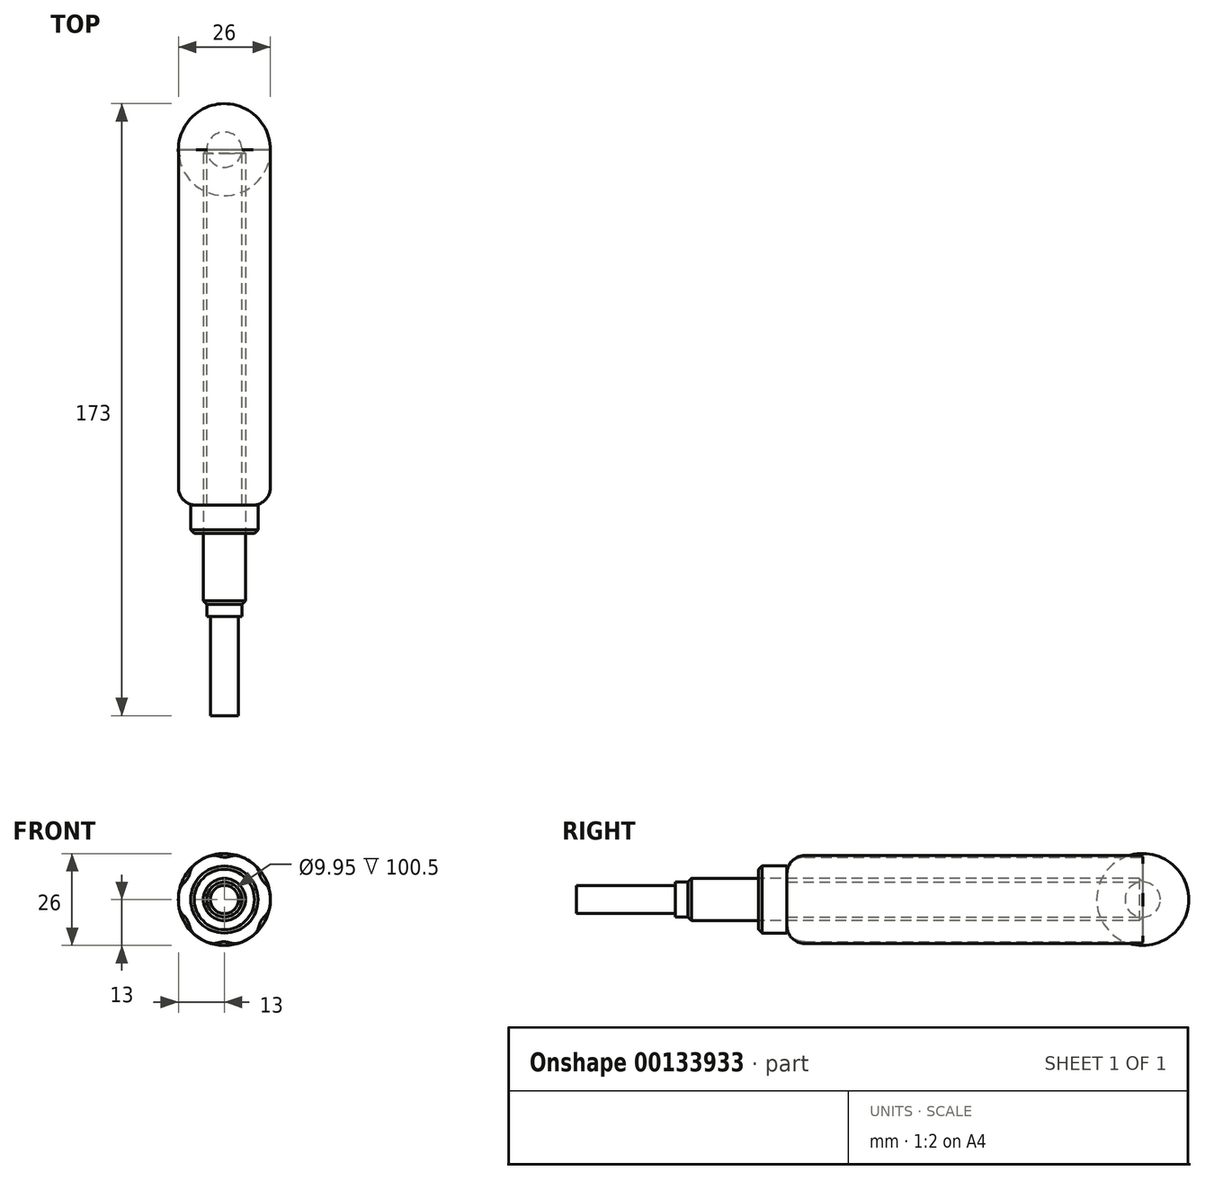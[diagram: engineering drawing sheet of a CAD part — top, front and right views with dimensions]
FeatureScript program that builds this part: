
annotation { "Feature Type Name" : "Feature", "Feature Type Description" : "" }
export const myFeature = defineFeature(function(context is Context, id is Id, definition is map)
    precondition{}
    {
        {
            var Q0;
            Q0=qCreatedBy(makeId("Front.planeOp"),FACE);
            var sketch = newSketch(context, id + "F0", { "sketchPlane" : qUnion([Q0])});
            skCircle(sketch, "E0", {"center": v(0, 0) * mm, "radius": 3.98 * mm});
            skSolve(sketch);
        }
        {
            var Q0;
            Q0 = qSketchRegion(id + "F0", true);
            extrude(context, id + "F1", {"entities" : qUnion([Q0]), "oppositeDirection" : true, "depth" : 28 * mm});
        }
        {
            var Q0;
            Q0=makeQuery(id+"F1.opExtrude","CAP_FACE",FACE,{"disambiguationData":[OSD([sQuery(id+"F0.wireOp",EDGE,"E0")])],"isStart":false});
            var sketch = newSketch(context, id + "F2", { "sketchPlane" : qUnion([Q0])});
            skCircle(sketch, "E1", {"center": v(0, 0) * mm, "radius": 4.92 * mm});
            skSolve(sketch);
        }
        {
            var Q0;
            Q0 = qSketchRegion(id + "F2", true);
            extrude(context, id + "F3", {"entities" : qUnion([Q0]), "operationType" : NewBodyOperationType.ADD, "depth" : 3.5 * mm});
        }
        {
            var Q0;
            Q0=makeQuery(id+"F3.opExtrude","CAP_FACE",FACE,{"disambiguationData":[OSD([sQuery(id+"F2.wireOp",EDGE,"E1")])],"isStart":false});
            var sketch = newSketch(context, id + "F4", { "sketchPlane" : qUnion([Q0])});
            skCircle(sketch, "E2", {"center": v(0, 0) * mm, "radius": 5.97 * mm});
            skSolve(sketch);
        }
        {
            var Q0;
            Q0 = qSketchRegion(id + "F4", true);
            extrude(context, id + "F5", {"entities" : qUnion([Q0]), "operationType" : NewBodyOperationType.ADD, "depth" : 128.5 * mm});
        }
        {
            var Q0;
            Q0=makeQuery(id+"F5.opExtrude","SWEPT_FACE",FACE,{"disambiguationData":[OSD([sQuery(id+"F4.wireOp",EDGE,"E2")])]});
            chamfer(context, id + "F6", {"entities" : qUnion([Q0]), "chamferType" : ChamferType.OFFSET_ANGLE, "width" : 1 * mm, "oppositeDirection" : false, "angle" : 45 * degree, "tangentPropagation" : true});
        }
        {
            var Q0;
            Q0=makeQuery(id+"F5.opExtrude","CAP_FACE",FACE,{"disambiguationData":[OSD([sQuery(id+"F4.wireOp",EDGE,"E2")])],"isStart":false});
            var sketch = newSketch(context, id + "F7", { "sketchPlane" : qUnion([Q0])});
            skCircle(sketch, "E3", {"center": v(0, 0) * mm, "radius": 13 * mm});
            skArc(sketch, "E4", {"start": v(-2.72, 12.71) * mm, "mid": v(-0.07, 11.97) * mm, "end": v(2.57, 12.74) * mm});
            skArc(sketch, "E5.1.0", {"start": v(-12.37, 4) * mm, "mid": v(-10.4, 5.93) * mm, "end": v(-9.75, 8.6) * mm});
            skArc(sketch, "E5.2.0", {"start": v(-9.65, -8.71) * mm, "mid": v(-10.33, -6.04) * mm, "end": v(-12.32, -4.14) * mm});
            skArc(sketch, "E5.3.0", {"start": v(2.72, -12.71) * mm, "mid": v(0.07, -11.97) * mm, "end": v(-2.57, -12.74) * mm});
            skArc(sketch, "E5.4.0", {"start": v(12.37, -4) * mm, "mid": v(10.4, -5.93) * mm, "end": v(9.75, -8.6) * mm});
            skArc(sketch, "E5.5.0", {"start": v(9.65, 8.71) * mm, "mid": v(10.33, 6.04) * mm, "end": v(12.32, 4.14) * mm});
            skSolve(sketch);
        }
        {
            var Q0;
            {var subQ5=sQuery(id+"F7.wireOp",EDGE,"E4");Q0=makeQuery(id+"F7.imprint","IMPRINT",FACE,{"disambiguationData":[TD([[makeQuery(id+"F7.imprint","IMPRINT",EDGE,{"derivedFrom":subQ5}),-1.0]])]});}
            extrude(context, id + "F8", {"entities" : qUnion([Q0]), "oppositeDirection" : true, "depth" : 100.5 * mm});
        }
        {
            var Q0;
            Q0=makeQuery(id+"F8.opExtrude","CAP_FACE",FACE,{"disambiguationData":[OSD([sQuery(id+"F4.wireOp",EDGE,"E2"),sQuery(id+"F7.wireOp",EDGE,"E3"),sQuery(id+"F7.wireOp",EDGE,"E4"),sQuery(id+"F7.wireOp",EDGE,"E5.1.0"),sQuery(id+"F7.wireOp",EDGE,"E5.2.0"),sQuery(id+"F7.wireOp",EDGE,"E5.3.0"),sQuery(id+"F7.wireOp",EDGE,"E5.4.0"),sQuery(id+"F7.wireOp",EDGE,"E5.5.0")])],"isStart":false});
            var sketch = newSketch(context, id + "F9", { "sketchPlane" : qUnion([Q0])});
            skCircle(sketch, "E6", {"center": v(0, 0) * mm, "radius": 9.5 * mm});
            skSolve(sketch);
        }
        {
            var Q0;
            Q0 = qSketchRegion(id + "F9", true);
            extrude(context, id + "F10", {"entities" : qUnion([Q0]), "depth" : 8 * mm});
        }
        {
            var Q0;
            Q0=makeQuery(id+"F10.opExtrude","CAP_EDGE",EDGE,{"disambiguationData":[OSD([sQuery(id+"F9.wireOp",EDGE,"E6")])],"isStart":false});
            chamfer(context, id + "F11", {"entities" : qUnion([Q0]), "width" : 1 * mm, "tangentPropagation" : true});
        }
        {
            var Q0;
            {var subQ0=sQuery(id+"F4.wireOp",EDGE,"E2");Q0=makeQuery(id+"F8.boolean.opBoolean","MERGE",FACE,{"derivedFrom":[makeQuery(id+"F5.opExtrude","CAP_FACE",FACE,{"disambiguationData":[OSD([subQ0])],"isStart":false}),makeQuery(id+"F8.opExtrude","CAP_FACE",FACE,{"disambiguationData":[OSD([subQ0,sQuery(id+"F7.wireOp",EDGE,"E3"),sQuery(id+"F7.wireOp",EDGE,"E4"),sQuery(id+"F7.wireOp",EDGE,"E5.1.0"),sQuery(id+"F7.wireOp",EDGE,"E5.2.0"),sQuery(id+"F7.wireOp",EDGE,"E5.3.0"),sQuery(id+"F7.wireOp",EDGE,"E5.4.0"),sQuery(id+"F7.wireOp",EDGE,"E5.5.0")])],"isStart":true})]});}
            var sketch = newSketch(context, id + "F12", { "sketchPlane" : qUnion([Q0])});
            skCircle(sketch, "E7", {"center": v(0, 0) * mm, "radius": 13 * mm});
            skLineSegment(sketch, "E8", {"start": v(-13, -0.07) * mm, "end": v(13, 0.07) * mm, "construction": true});
            skLineSegment(sketch, "E9", {"start": v(-13, -0.07) * mm, "end": v(13, 0.07) * mm});
            skSolve(sketch);
        }
        {
            var Q0;
            {var subQ2=sQuery(id+"F12.wireOp",EDGE,"E9");Q0=makeQuery(id+"F12.imprint","IMPRINT",FACE,{"disambiguationData":[TD([[makeQuery(id+"F12.imprint","IMPRINT",EDGE,{"derivedFrom":subQ2}),-1.0]])]});}
            var Q1;
            {var subQ1=makeQuery(id+"F8.opExtrude","CAP_EDGE",EDGE,{"disambiguationData":[OSD([sQuery(id+"F7.wireOp",EDGE,"E5.4.0")])],"isStart":true});Q1=makeQuery(id+"F12.imprint","IMPRINT",FACE,{"disambiguationData":[TD([[makeQuery(id+"F12.imprint","IMPRINT",EDGE,{"derivedFrom":subQ1}),1.0]])]});}
            var Q2;
            {var subQ1=makeQuery(id+"F8.opExtrude","CAP_EDGE",EDGE,{"disambiguationData":[OSD([sQuery(id+"F7.wireOp",EDGE,"E5.3.0")])],"isStart":true});Q2=makeQuery(id+"F12.imprint","IMPRINT",FACE,{"disambiguationData":[TD([[makeQuery(id+"F12.imprint","IMPRINT",EDGE,{"derivedFrom":subQ1}),1.0]])]});}
            var Q3;
            {var subQ1=makeQuery(id+"F8.opExtrude","CAP_EDGE",EDGE,{"disambiguationData":[OSD([sQuery(id+"F7.wireOp",EDGE,"E5.2.0")])],"isStart":true});Q3=makeQuery(id+"F12.imprint","IMPRINT",FACE,{"disambiguationData":[TD([[makeQuery(id+"F12.imprint","IMPRINT",EDGE,{"derivedFrom":subQ1}),1.0]])]});}
            var Q4;
            Q4=sQuery(id+"F12.wireOp",EDGE,"E8");
            revolve(context, id + "F13", {"entities" : qUnion([Q0, Q1, Q2, Q3]), "axis" : qUnion([Q4]), "revolveType" : RevolveType.FULL});
        }
        {
            var Q0;
            {var subQ0=sQuery(id+"F7.wireOp",EDGE,"E5.4.0");var subQ1=sQuery(id+"F7.wireOp",EDGE,"E3");Q0=makeQuery(id+"F8.opExtrude","SWEPT_EDGE",EDGE,{"disambiguationData":[OSD([subQ1,subQ0]),TDD([makeQuery(id+"F7.imprint","INTERSECT",VERTEX,{"disambiguationData":[OD(0.0)],"derivedFrom":[subQ1,subQ0]})])]});}
            var Q1;
            {var subQ0=sQuery(id+"F7.wireOp",EDGE,"E5.4.0");var subQ1=sQuery(id+"F7.wireOp",EDGE,"E3");Q1=makeQuery(id+"F8.opExtrude","SWEPT_EDGE",EDGE,{"disambiguationData":[OSD([subQ1,subQ0]),TDD([makeQuery(id+"F7.imprint","INTERSECT",VERTEX,{"disambiguationData":[OD(1.0)],"derivedFrom":[subQ1,subQ0]})])]});}
            var Q2;
            {var subQ0=sQuery(id+"F7.wireOp",EDGE,"E5.5.0");var subQ1=sQuery(id+"F7.wireOp",EDGE,"E3");Q2=makeQuery(id+"F8.opExtrude","SWEPT_EDGE",EDGE,{"disambiguationData":[OSD([subQ1,subQ0]),TDD([makeQuery(id+"F7.imprint","INTERSECT",VERTEX,{"disambiguationData":[OD(1.0)],"derivedFrom":[subQ1,subQ0]})])]});}
            var Q3;
            {var subQ0=sQuery(id+"F7.wireOp",EDGE,"E5.5.0");var subQ1=sQuery(id+"F7.wireOp",EDGE,"E3");Q3=makeQuery(id+"F8.opExtrude","SWEPT_EDGE",EDGE,{"disambiguationData":[OSD([subQ1,subQ0]),TDD([makeQuery(id+"F7.imprint","INTERSECT",VERTEX,{"disambiguationData":[OD(0.0)],"derivedFrom":[subQ1,subQ0]})])]});}
            var Q4;
            {var subQ0=sQuery(id+"F7.wireOp",EDGE,"E4");var subQ1=sQuery(id+"F7.wireOp",EDGE,"E3");Q4=makeQuery(id+"F8.opExtrude","SWEPT_EDGE",EDGE,{"disambiguationData":[OSD([subQ1,subQ0]),TDD([makeQuery(id+"F7.imprint","INTERSECT",VERTEX,{"disambiguationData":[OD(1.0)],"derivedFrom":[subQ1,subQ0]})])]});}
            var Q5;
            {var subQ0=sQuery(id+"F7.wireOp",EDGE,"E4");var subQ1=sQuery(id+"F7.wireOp",EDGE,"E3");Q5=makeQuery(id+"F8.opExtrude","SWEPT_EDGE",EDGE,{"disambiguationData":[OSD([subQ1,subQ0]),TDD([makeQuery(id+"F7.imprint","INTERSECT",VERTEX,{"disambiguationData":[OD(0.0)],"derivedFrom":[subQ1,subQ0]})])]});}
            var Q6;
            {var subQ0=sQuery(id+"F7.wireOp",EDGE,"E5.1.0");var subQ1=sQuery(id+"F7.wireOp",EDGE,"E3");Q6=makeQuery(id+"F8.opExtrude","SWEPT_EDGE",EDGE,{"disambiguationData":[OSD([subQ1,subQ0]),TDD([makeQuery(id+"F7.imprint","INTERSECT",VERTEX,{"disambiguationData":[OD(1.0)],"derivedFrom":[subQ1,subQ0]})])]});}
            var Q7;
            {var subQ0=sQuery(id+"F7.wireOp",EDGE,"E5.1.0");var subQ1=sQuery(id+"F7.wireOp",EDGE,"E3");Q7=makeQuery(id+"F8.opExtrude","SWEPT_EDGE",EDGE,{"disambiguationData":[OSD([subQ1,subQ0]),TDD([makeQuery(id+"F7.imprint","INTERSECT",VERTEX,{"disambiguationData":[OD(0.0)],"derivedFrom":[subQ1,subQ0]})])]});}
            var Q8;
            {var subQ0=sQuery(id+"F7.wireOp",EDGE,"E5.2.0");var subQ1=sQuery(id+"F7.wireOp",EDGE,"E3");Q8=makeQuery(id+"F8.opExtrude","SWEPT_EDGE",EDGE,{"disambiguationData":[OSD([subQ1,subQ0]),TDD([makeQuery(id+"F7.imprint","INTERSECT",VERTEX,{"disambiguationData":[OD(1.0)],"derivedFrom":[subQ1,subQ0]})])]});}
            var Q9;
            {var subQ0=sQuery(id+"F7.wireOp",EDGE,"E5.2.0");var subQ1=sQuery(id+"F7.wireOp",EDGE,"E3");Q9=makeQuery(id+"F8.opExtrude","SWEPT_EDGE",EDGE,{"disambiguationData":[OSD([subQ1,subQ0]),TDD([makeQuery(id+"F7.imprint","INTERSECT",VERTEX,{"disambiguationData":[OD(0.0)],"derivedFrom":[subQ1,subQ0]})])]});}
            var Q10;
            {var subQ0=sQuery(id+"F7.wireOp",EDGE,"E5.3.0");var subQ1=sQuery(id+"F7.wireOp",EDGE,"E3");Q10=makeQuery(id+"F8.opExtrude","SWEPT_EDGE",EDGE,{"disambiguationData":[OSD([subQ1,subQ0]),TDD([makeQuery(id+"F7.imprint","INTERSECT",VERTEX,{"disambiguationData":[OD(1.0)],"derivedFrom":[subQ1,subQ0]})])]});}
            var Q11;
            {var subQ0=sQuery(id+"F7.wireOp",EDGE,"E5.3.0");var subQ1=sQuery(id+"F7.wireOp",EDGE,"E3");Q11=makeQuery(id+"F8.opExtrude","SWEPT_EDGE",EDGE,{"disambiguationData":[OSD([subQ1,subQ0]),TDD([makeQuery(id+"F7.imprint","INTERSECT",VERTEX,{"disambiguationData":[OD(0.0)],"derivedFrom":[subQ1,subQ0]})])]});}
            fillet(context, id + "F14", {"entities" : qUnion([Q0, Q1, Q2, Q3, Q4, Q5, Q6, Q7, Q8, Q9, Q10, Q11]), "radius" : 5 * mm, "tangentPropagation" : true, "allowEdgeOverflow" : false});
        }
        {
            var Q0;
            {var subQ0=sQuery(id+"F7.wireOp",EDGE,"E3");Q0=makeQuery(id+"F8.opExtrude","CAP_EDGE",EDGE,{"disambiguationData":[OSD([subQ0]),TDD([makeQuery(id+"F7.imprint","IMPRINT",EDGE,{"disambiguationData":[TD([[makeQuery(id+"F7.imprint","INTERSECT",VERTEX,{"disambiguationData":[OD(0.0)],"derivedFrom":[subQ0,sQuery(id+"F7.wireOp",EDGE,"E5.2.0")]}),-1.0]])],"derivedFrom":subQ0})])],"isStart":false});}
            fillet(context, id + "F15", {"entities" : qUnion([Q0]), "radius" : 5 * mm, "tangentPropagation" : true, "allowEdgeOverflow" : false});
        }
    });
